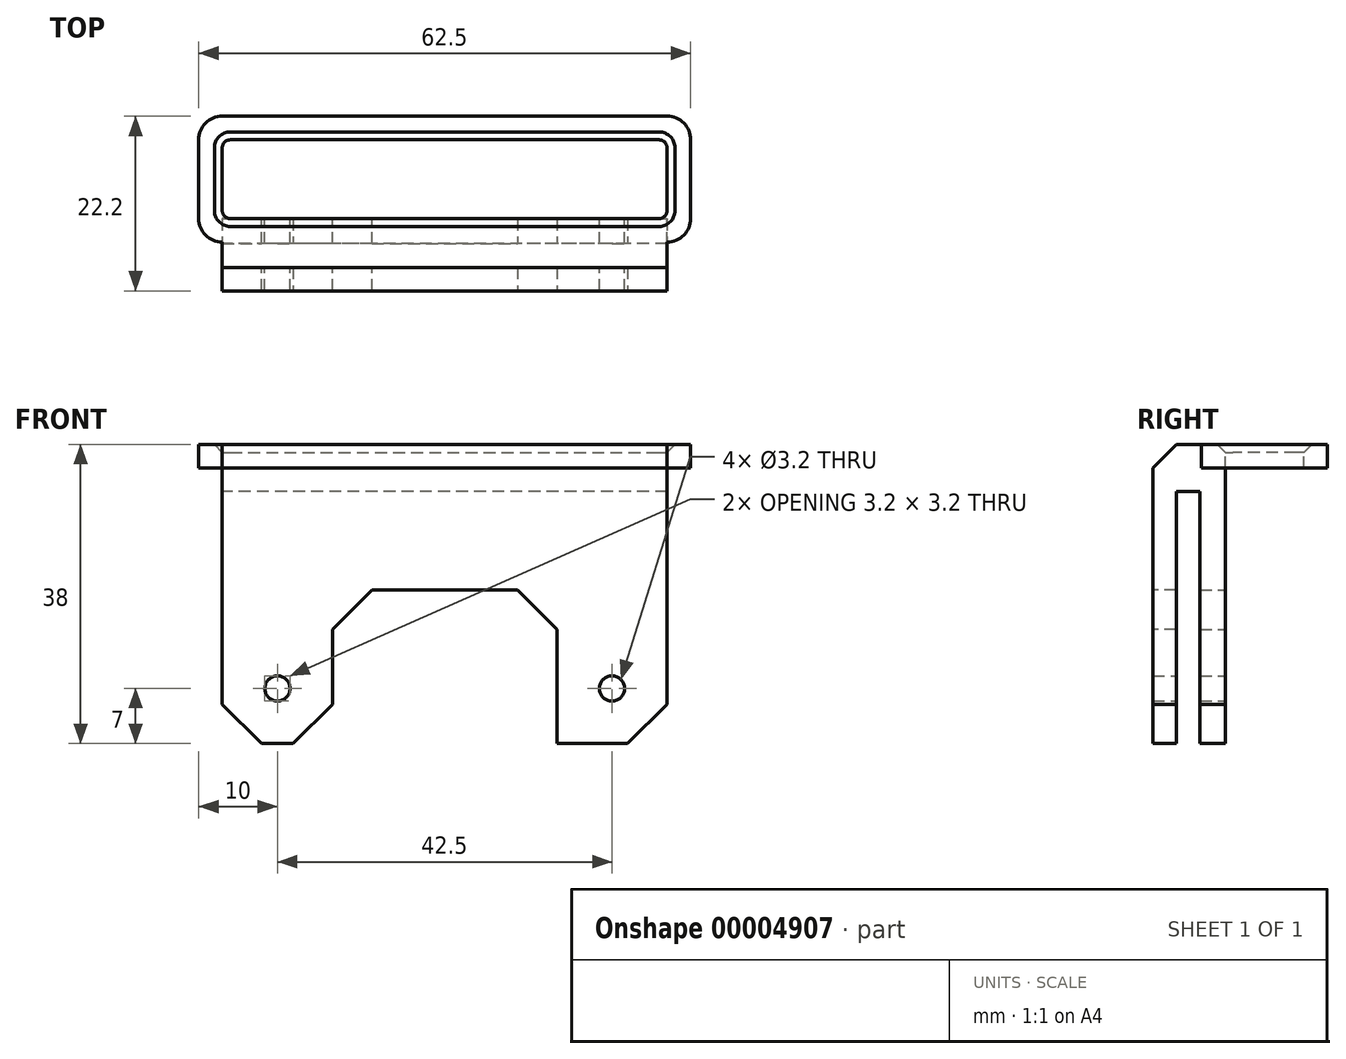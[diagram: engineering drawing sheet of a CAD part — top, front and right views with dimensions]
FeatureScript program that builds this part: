
annotation { "Feature Type Name" : "Feature", "Feature Type Description" : "" }
export const myFeature = defineFeature(function(context is Context, id is Id, definition is map)
    precondition{}
    {
        {
            var Q0;
            Q0=qCreatedBy(makeId("Right.planeOp"),FACE);
            var sketch = newSketch(context, id + "F0", { "sketchPlane" : qUnion([Q0])});
            skLineSegment(sketch, "E0", {"start": v(0, 0) * mm, "end": v(0, 38) * mm});
            skLineSegment(sketch, "E1", {"start": v(0, 38) * mm, "end": v(9.2, 38) * mm});
            skLineSegment(sketch, "E2", {"start": v(9.2, 38) * mm, "end": v(9.2, 0) * mm});
            skLineSegment(sketch, "E3", {"start": v(9.2, 0) * mm, "end": v(6, 0) * mm});
            skLineSegment(sketch, "E4", {"start": v(6, 0) * mm, "end": v(6, 32) * mm});
            skLineSegment(sketch, "E5", {"start": v(6, 32) * mm, "end": v(3, 32) * mm});
            skLineSegment(sketch, "E6", {"start": v(3, 32) * mm, "end": v(3, 0) * mm});
            skLineSegment(sketch, "E7", {"start": v(3, 0) * mm, "end": v(0, 0) * mm});
            skSolve(sketch);
        }
        {
            var Q0;
            Q0 = qSketchRegion(id + "F0", true);
            extrude(context, id + "F1", {"entities" : qUnion([Q0]), "endBound" : BoundingType.SYMMETRIC, "depth" : 56.5 * mm});
        }
        {
            var Q0;
            Q0=makeQuery(id+"F1.opExtrude","SWEPT_FACE",FACE,{"disambiguationData":[OSD([sQuery(id+"F0.wireOp",EDGE,"E2")])]});
            var sketch = newSketch(context, id + "F2", { "sketchPlane" : qUnion([Q0])});
            skCircle(sketch, "E8", {"center": v(-21.25, 7) * mm, "radius": 1.6 * mm});
            skCircle(sketch, "E9", {"center": v(21.25, 7) * mm, "radius": 1.6 * mm});
            skPoint(sketch, "E10", {"position": v(-28.25, 38) * mm});
            skPoint(sketch, "E11", {"position": v(-28.25, 32) * mm});
            skPoint(sketch, "E12", {"position": v(0, 38) * mm});
            skSolve(sketch);
        }
        {
            var Q0;
            Q0=makeQuery(id+"F1.opExtrude","SWEPT_FACE",FACE,{"disambiguationData":[OSD([sQuery(id+"F0.wireOp",EDGE,"E1")])]});
            var sketch = newSketch(context, id + "F3", { "sketchPlane" : qUnion([Q0])});
            skLineSegment(sketch, "E13", {"start": v(-28.25, 0) * mm, "end": v(-28.25, 6.2) * mm});
            skLineSegment(sketch, "E14", {"start": v(-28.25, 6.2) * mm, "end": v(-28.25, 6.2) * mm});
            skLineSegment(sketch, "E15", {"start": v(-31.25, 9.2) * mm, "end": v(-31.25, 19.2) * mm});
            skLineSegment(sketch, "E16", {"start": v(-28.25, 22.2) * mm, "end": v(28.25, 22.2) * mm});
            skLineSegment(sketch, "E17", {"start": v(31.25, 19.2) * mm, "end": v(31.25, 9.2) * mm});
            skLineSegment(sketch, "E18", {"start": v(28.25, 6.2) * mm, "end": v(28.25, 6.2) * mm});
            skLineSegment(sketch, "E19", {"start": v(28.25, 6.2) * mm, "end": v(28.25, 0) * mm});
            skLineSegment(sketch, "E20", {"start": v(28.25, 0) * mm, "end": v(-28.25, 0) * mm});
            skLineSegment(sketch, "E21.bottom", {"start": v(-27.25, 9.2) * mm, "end": v(27.25, 9.2) * mm});
            skLineSegment(sketch, "E21.top", {"start": v(-27.25, 19.2) * mm, "end": v(27.25, 19.2) * mm});
            skLineSegment(sketch, "E21.left", {"start": v(-28.25, 10.2) * mm, "end": v(-28.25, 18.2) * mm});
            skLineSegment(sketch, "E21.right", {"start": v(28.25, 10.2) * mm, "end": v(28.25, 18.2) * mm});
            skPoint(sketch, "E22.visualSharp", {"position": v(-28.25, 19.2) * mm});
            skArc(sketch, "E22.filletArc", {"start": v(-27.25, 19.2) * mm, "mid": v(-27.96, 18.9) * mm, "end": v(-28.25, 18.2) * mm});
            skPoint(sketch, "E23.visualSharp", {"position": v(-28.25, 9.2) * mm});
            skArc(sketch, "E23.filletArc", {"start": v(-28.25, 10.2) * mm, "mid": v(-27.96, 9.5) * mm, "end": v(-27.25, 9.2) * mm});
            skPoint(sketch, "E24.visualSharp", {"position": v(28.25, 9.2) * mm});
            skArc(sketch, "E24.filletArc", {"start": v(27.25, 9.2) * mm, "mid": v(27.96, 9.5) * mm, "end": v(28.25, 10.2) * mm});
            skPoint(sketch, "E25.visualSharp", {"position": v(28.25, 19.2) * mm});
            skArc(sketch, "E25.filletArc", {"start": v(28.25, 18.2) * mm, "mid": v(27.96, 18.9) * mm, "end": v(27.25, 19.2) * mm});
            skPoint(sketch, "E26.visualSharp", {"position": v(-31.25, 22.2) * mm});
            skArc(sketch, "E26.filletArc", {"start": v(-28.25, 22.2) * mm, "mid": v(-30.37, 21.32) * mm, "end": v(-31.25, 19.2) * mm});
            skPoint(sketch, "E27.visualSharp", {"position": v(-31.25, 6.2) * mm});
            skArc(sketch, "E27.filletArc", {"start": v(-31.25, 9.2) * mm, "mid": v(-30.37, 7.08) * mm, "end": v(-28.25, 6.2) * mm});
            skPoint(sketch, "E28.visualSharp", {"position": v(31.25, 22.2) * mm});
            skArc(sketch, "E28.filletArc", {"start": v(31.25, 19.2) * mm, "mid": v(30.37, 21.32) * mm, "end": v(28.25, 22.2) * mm});
            skPoint(sketch, "E29.visualSharp", {"position": v(31.25, 6.2) * mm});
            skArc(sketch, "E29.filletArc", {"start": v(28.25, 6.2) * mm, "mid": v(30.37, 7.08) * mm, "end": v(31.25, 9.2) * mm});
            skSolve(sketch);
        }
        {
            var Q0;
            {var subQ8=sQuery(id+"F3.wireOp",EDGE,"E13");Q0=makeQuery(id+"F3.imprint","IMPRINT",FACE,{"disambiguationData":[TD([[makeQuery(id+"F3.imprint","IMPRINT",EDGE,{"derivedFrom":subQ8}),-1.0]])]});}
            var Q1;
            Q1=makeQuery(id+"F3.imprint","IMPRINT",FACE,{"disambiguationData":[TD([[makeQuery(id+"F3.imprint","IMPRINT",EDGE,{"derivedFrom":sQuery(id+"F3.wireOp",EDGE,"E15")}),-1.0]])]});
            extrude(context, id + "F4", {"entities" : qUnion([Q0, Q1]), "operationType" : NewBodyOperationType.ADD, "oppositeDirection" : true, "depth" : 3 * mm});
        }
        {
            var Q0;
            Q0=makeQuery(id+"F4.opExtrude","CAP_EDGE",EDGE,{"disambiguationData":[OSD([sQuery(id+"F3.wireOp",EDGE,"E23.filletArc")])],"isStart":true});
            var Q1;
            Q1=makeQuery(id+"F4.opExtrude","CAP_EDGE",EDGE,{"disambiguationData":[OSD([sQuery(id+"F3.wireOp",EDGE,"E21.left")])],"isStart":true});
            var Q2;
            Q2=makeQuery(id+"F4.opExtrude","CAP_EDGE",EDGE,{"disambiguationData":[OSD([sQuery(id+"F3.wireOp",EDGE,"E22.filletArc")])],"isStart":true});
            var Q3;
            Q3=makeQuery(id+"F4.opExtrude","CAP_EDGE",EDGE,{"disambiguationData":[OSD([sQuery(id+"F3.wireOp",EDGE,"E21.top")])],"isStart":true});
            var Q4;
            Q4=makeQuery(id+"F1.opExtrude","SWEPT_EDGE",EDGE,{"disambiguationData":[OSD([sQuery(id+"F0.wireOp",EDGE,"E1"),sQuery(id+"F0.wireOp",EDGE,"E2")])]});
            var Q5;
            Q5=makeQuery(id+"F4.opExtrude","CAP_EDGE",EDGE,{"disambiguationData":[OSD([sQuery(id+"F3.wireOp",EDGE,"E21.right")])],"isStart":true});
            var Q6;
            Q6=makeQuery(id+"F4.opExtrude","CAP_EDGE",EDGE,{"disambiguationData":[OSD([sQuery(id+"F3.wireOp",EDGE,"E25.filletArc")])],"isStart":true});
            var Q7;
            Q7=makeQuery(id+"F4.opExtrude","CAP_EDGE",EDGE,{"disambiguationData":[OSD([sQuery(id+"F3.wireOp",EDGE,"E24.filletArc")])],"isStart":true});
            chamfer(context, id + "F5", {"entities" : qUnion([Q0, Q1, Q2, Q3, Q4, Q5, Q6, Q7]), "width" : 1 * mm, "tangentPropagation" : true});
        }
        {
            var Q0;
            Q0=makeQuery(id+"F1.opExtrude","SWEPT_EDGE",EDGE,{"disambiguationData":[OSD([sQuery(id+"F0.wireOp",EDGE,"E0"),sQuery(id+"F0.wireOp",EDGE,"E1")])]});
            chamfer(context, id + "F6", {"entities" : qUnion([Q0]), "width" : 3 * mm, "tangentPropagation" : true});
        }
        {
            var Q0;
            Q0=makeQuery(id+"F1.opExtrude","CAP_EDGE",EDGE,{"disambiguationData":[OSD([sQuery(id+"F0.wireOp",EDGE,"E7")])],"isStart":false});
            var Q1;
            Q1=makeQuery(id+"F1.opExtrude","CAP_EDGE",EDGE,{"disambiguationData":[OSD([sQuery(id+"F0.wireOp",EDGE,"E3")])],"isStart":false});
            var Q2;
            Q2=makeQuery(id+"F1.opExtrude","CAP_EDGE",EDGE,{"disambiguationData":[OSD([sQuery(id+"F0.wireOp",EDGE,"E3")])],"isStart":true});
            var Q3;
            Q3=makeQuery(id+"F1.opExtrude","CAP_EDGE",EDGE,{"disambiguationData":[OSD([sQuery(id+"F0.wireOp",EDGE,"E7")])],"isStart":true});
            chamfer(context, id + "F7", {"entities" : qUnion([Q0, Q1, Q2, Q3]), "width" : 5 * mm, "tangentPropagation" : true});
        }
        {
            var Q0;
            Q0 = qSketchRegion(id + "F2", true);
            extrude(context, id + "F8", {"entities" : qUnion([Q0]), "operationType" : NewBodyOperationType.REMOVE, "endBound" : BoundingType.THROUGH_ALL, "oppositeDirection" : true, "depth" : 25 * mm});
        }
        {
            var Q0;
            Q0=makeQuery(id+"F1.opExtrude","SWEPT_FACE",FACE,{"disambiguationData":[OSD([sQuery(id+"F0.wireOp",EDGE,"E0")])]});
            var sketch = newSketch(context, id + "F9", { "sketchPlane" : qUnion([Q0])});
            skLineSegment(sketch, "E30", {"start": v(-14.25, 0) * mm, "end": v(-14.25, 19.5) * mm});
            skLineSegment(sketch, "E31", {"start": v(-14.25, 19.5) * mm, "end": v(14.25, 19.5) * mm});
            skLineSegment(sketch, "E32", {"start": v(14.25, 19.5) * mm, "end": v(14.25, 0) * mm});
            skLineSegment(sketch, "E33", {"start": v(14.25, 0) * mm, "end": v(-14.25, 0) * mm});
            skSolve(sketch);
        }
        {
            var Q0;
            Q0 = qSketchRegion(id + "F9", true);
            var Q1;
            Q1=makeQuery(id+"F1.opExtrude","SWEPT_FACE",FACE,{"disambiguationData":[OSD([sQuery(id+"F0.wireOp",EDGE,"E2")])]});
            extrude(context, id + "F10", {"entities" : qUnion([Q0]), "operationType" : NewBodyOperationType.REMOVE, "endBound" : BoundingType.UP_TO_SURFACE, "oppositeDirection" : true, "endBoundEntityFace" : qUnion([Q1]), "depth" : 25 * mm});
        }
        {
            var Q0;
            Q0=makeQuery(id+"F10.boolean.opBoolean","COPY",EDGE,{"derivedFrom":makeQuery(id+"F10.opExtrude","SWEPT_EDGE",EDGE,{"disambiguationData":[OSD([sQuery(id+"F0.wireOp",EDGE,"E0"),sQuery(id+"F0.wireOp",EDGE,"E7"),sQuery(id+"F9.wireOp",EDGE,"E30"),sQuery(id+"F9.wireOp",EDGE,"E33")])]})});
            var Q1;
            Q1=makeQuery(id+"F10.boolean.opBoolean","COPY",EDGE,{"derivedFrom":makeQuery(id+"F10.opExtrude","SWEPT_EDGE",EDGE,{"disambiguationData":[OSD([sQuery(id+"F9.wireOp",EDGE,"E30"),sQuery(id+"F9.wireOp",EDGE,"E31")])]})});
            var Q2;
            Q2=makeQuery(id+"F10.boolean.opBoolean","COPY",EDGE,{"derivedFrom":makeQuery(id+"F10.opExtrude","SWEPT_EDGE",EDGE,{"disambiguationData":[OSD([sQuery(id+"F0.wireOp",EDGE,"E0"),sQuery(id+"F0.wireOp",EDGE,"E7"),sQuery(id+"F9.wireOp",EDGE,"E32"),sQuery(id+"F9.wireOp",EDGE,"E33")])]})});
            var Q3;
            Q3=makeQuery(id+"F10.boolean.opBoolean","COPY",EDGE,{"derivedFrom":makeQuery(id+"F10.opExtrude","SWEPT_EDGE",EDGE,{"disambiguationData":[OSD([sQuery(id+"F9.wireOp",EDGE,"E31"),sQuery(id+"F9.wireOp",EDGE,"E32")])]})});
            chamfer(context, id + "F11", {"entities" : qUnion([Q0, Q1, Q2, Q3]), "width" : 5 * mm, "tangentPropagation" : true});
        }
    });
